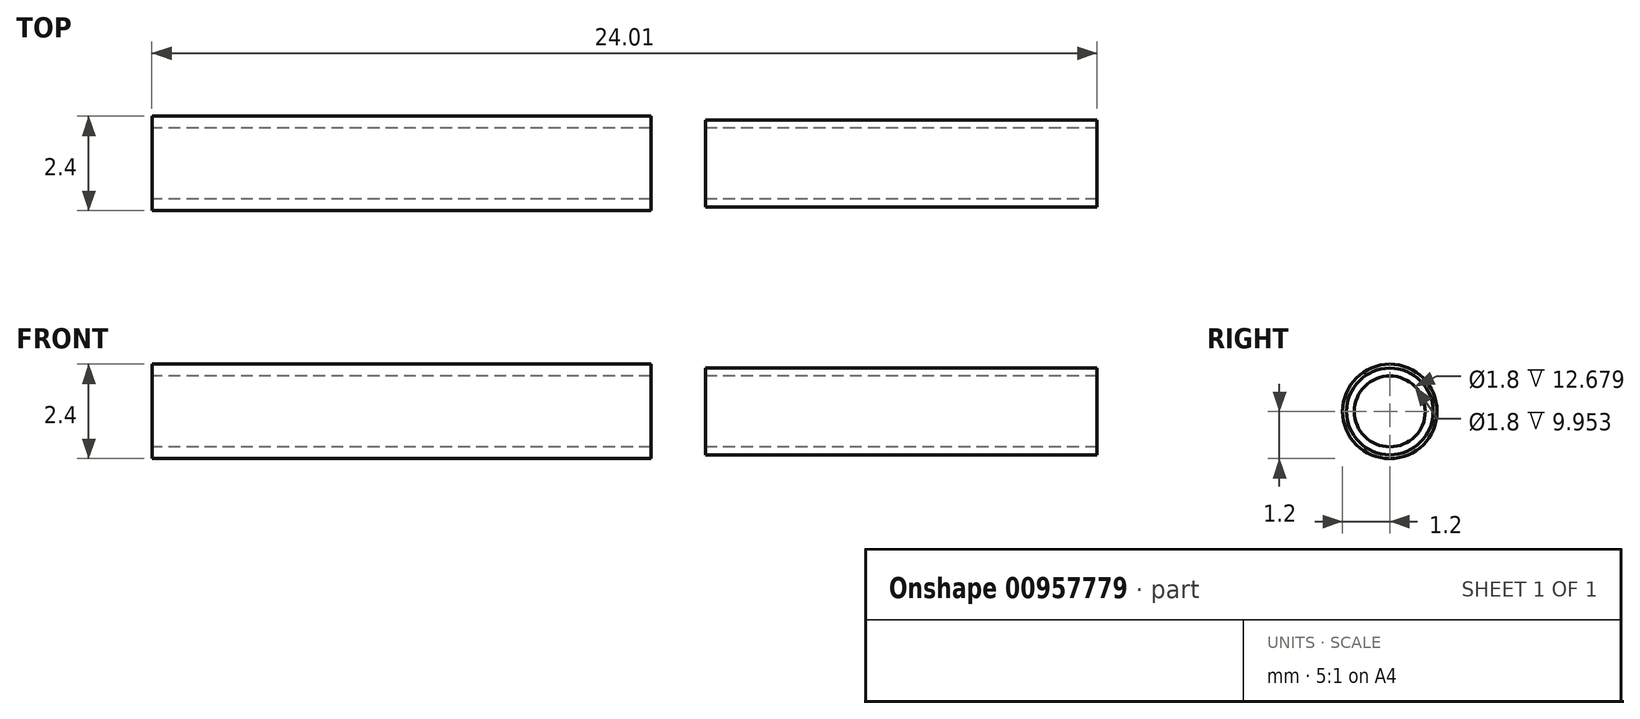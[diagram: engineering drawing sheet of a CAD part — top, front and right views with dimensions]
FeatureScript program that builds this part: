
annotation { "Feature Type Name" : "Feature", "Feature Type Description" : "" }
export const myFeature = defineFeature(function(context is Context, id is Id, definition is map)
    precondition{}
    {
        {
            var Q0;
            Q0=qCreatedBy(makeId("Top.planeOp"),FACE);
            var sketch = newSketch(context, id + "F0", { "sketchPlane" : qUnion([Q0])});
            skLineSegment(sketch, "E0", {"start": v(-12.5, 0) * mm, "end": v(12.27, 0) * mm, "construction": true});
            skLineSegment(sketch, "E1", {"start": v(-11.77, 1.2) * mm, "end": v(-11.77, 0.9) * mm});
            skLineSegment(sketch, "E2", {"start": v(-11.77, 0.9) * mm, "end": v(0.91, 0.9) * mm});
            skLineSegment(sketch, "E3", {"start": v(0.91, 0.9) * mm, "end": v(0.91, 1.2) * mm});
            skLineSegment(sketch, "E4", {"start": v(0.91, 1.2) * mm, "end": v(-11.77, 1.2) * mm});
            skLineSegment(sketch, "E5", {"start": v(2.29, 1.1) * mm, "end": v(2.29, 0.9) * mm});
            skLineSegment(sketch, "E6", {"start": v(2.29, 0.9) * mm, "end": v(12.24, 0.9) * mm});
            skLineSegment(sketch, "E7", {"start": v(12.24, 0.9) * mm, "end": v(12.24, 1.1) * mm});
            skLineSegment(sketch, "E8", {"start": v(12.24, 1.1) * mm, "end": v(2.29, 1.1) * mm});
            skSolve(sketch);
        }
        {
            var Q0;
            Q0 = qSketchRegion(id + "F0", true);
            var Q1;
            Q1=sQuery(id+"F0.wireOp",EDGE,"E0");
            revolve(context, id + "F1", {"surfaceOperationType" : NewSurfaceOperationType.NEW, "entities" : qUnion([Q0]), "axis" : qUnion([Q1]), "revolveType" : RevolveType.FULL});
        }
    });
